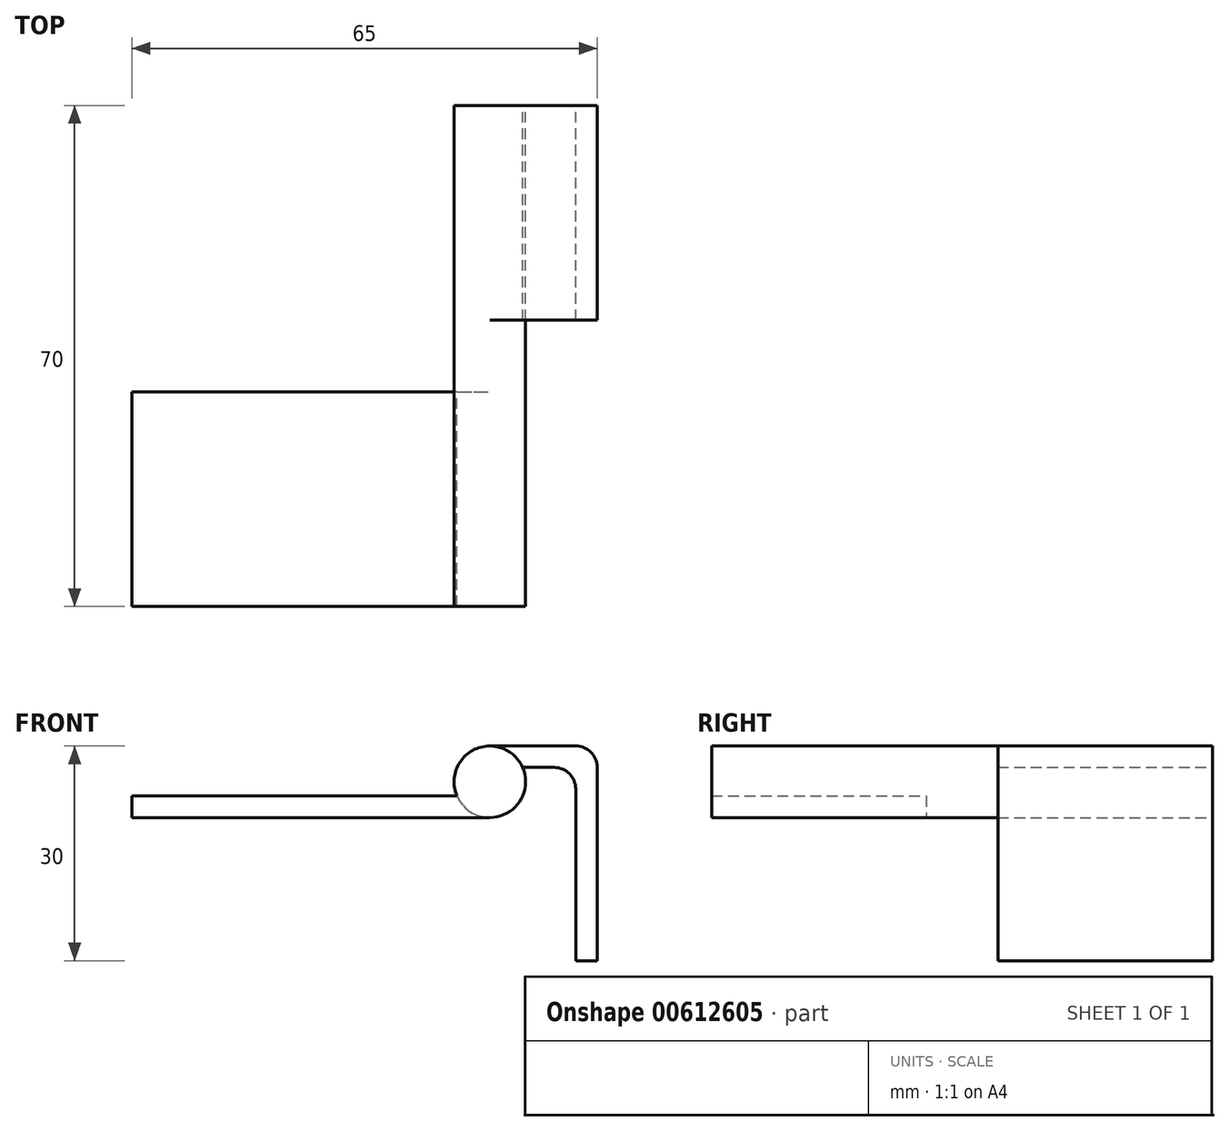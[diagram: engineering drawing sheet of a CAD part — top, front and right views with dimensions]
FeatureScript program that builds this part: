
annotation { "Feature Type Name" : "Feature", "Feature Type Description" : "" }
export const myFeature = defineFeature(function(context is Context, id is Id, definition is map)
    precondition{}
    {
        {
            var Q0;
            Q0=qCreatedBy(makeId("Front.planeOp"),FACE);
            var sketch = newSketch(context, id + "F0", { "sketchPlane" : qUnion([Q0])});
            skCircle(sketch, "E0", {"center": v(0, 0) * mm, "radius": 5 * mm});
            skLineSegment(sketch, "E1.0", {"start": v(0, 2) * mm, "end": v(9, 2) * mm});
            skLineSegment(sketch, "E2.0", {"start": v(0, 5) * mm, "end": v(12, 5) * mm});
            skLineSegment(sketch, "E3", {"start": v(0, 5) * mm, "end": v(0, 2) * mm});
            skLineSegment(sketch, "E4", {"start": v(15, 2) * mm, "end": v(15, 2) * mm});
            skLineSegment(sketch, "E5", {"start": v(-2, -70) * mm, "end": v(-5, -70) * mm});
            skLineSegment(sketch, "E6", {"start": v(15, -3) * mm, "end": v(15, -25) * mm});
            skLineSegment(sketch, "E7", {"start": v(15, -25) * mm, "end": v(12, -25) * mm});
            skLineSegment(sketch, "E8", {"start": v(12, -25) * mm, "end": v(12, -1) * mm});
            skPoint(sketch, "E9.newPointB", {"position": v(15, 2) * mm});
            skArc(sketch, "E9.filletArc", {"start": v(12, -1) * mm, "mid": v(11.12, 1.12) * mm, "end": v(9, 2) * mm});
            skPoint(sketch, "E10.visualSharp", {"position": v(15, 5) * mm});
            skArc(sketch, "E10.filletArc", {"start": v(15, 2) * mm, "mid": v(14.12, 4.12) * mm, "end": v(12, 5) * mm});
            skLineSegment(sketch, "E11", {"start": v(15, -3) * mm, "end": v(15, 2) * mm});
            skSolve(sketch);
        }
        {
            var Q0;
            {var subQ0=sQuery(id+"F0.wireOp",EDGE,"E3");Q0=makeQuery(id+"F0.imprint","IMPRINT",FACE,{"disambiguationData":[TD([[makeQuery(id+"F0.imprint","IMPRINT",EDGE,{"derivedFrom":subQ0}),-1.0]])]});}
            var Q1;
            {var subQ0=sQuery(id+"F0.wireOp",EDGE,"E3");Q1=makeQuery(id+"F0.imprint","IMPRINT",FACE,{"disambiguationData":[TD([[makeQuery(id+"F0.imprint","IMPRINT",EDGE,{"derivedFrom":subQ0}),1.0]])]});}
            extrude(context, id + "F1", {"entities" : qUnion([Q0, Q1]), "depth" : 70 * mm, "offsetDistance" : 25.4 * mm});
        }
        {
            var Q0;
            {var subQ0=sQuery(id+"F0.wireOp",EDGE,"E2.0");Q0=makeQuery(id+"F0.imprint","IMPRINT",FACE,{"disambiguationData":[TD([[makeQuery(id+"F0.imprint","IMPRINT",EDGE,{"derivedFrom":subQ0}),-1.0]])]});}
            extrude(context, id + "F2", {"entities" : qUnion([Q0]), "operationType" : NewBodyOperationType.ADD, "depth" : 30 * mm, "offsetDistance" : 25.4 * mm});
        }
        {
            var Q0;
            Q0=makeQuery(id+"F1.opExtrude","CAP_FACE",FACE,{"disambiguationData":[OSD([sQuery(id+"F0.wireOp",EDGE,"E0")])],"isStart":false});
            var sketch = newSketch(context, id + "F3", { "sketchPlane" : qUnion([Q0])});
            skLineSegment(sketch, "E12", {"start": v(0, -2) * mm, "end": v(-50, -2) * mm});
            skLineSegment(sketch, "E13", {"start": v(-50, -5) * mm, "end": v(0, -5) * mm});
            skLineSegment(sketch, "E14", {"start": v(-50, -2) * mm, "end": v(-50, -5) * mm});
            skLineSegment(sketch, "E15", {"start": v(0, -2) * mm, "end": v(0, -5) * mm});
            skSolve(sketch);
        }
        {
            var Q0;
            {var subQ0=sQuery(id+"F3.wireOp",EDGE,"E12");Q0=makeQuery(id+"F3.imprint","IMPRINT",FACE,{"disambiguationData":[TD([[makeQuery(id+"F3.imprint","IMPRINT",EDGE,{"derivedFrom":subQ0}),1.0]])]});}
            var Q1;
            {var subQ4=sQuery(id+"F3.wireOp",EDGE,"E13");Q1=makeQuery(id+"F3.imprint","IMPRINT",FACE,{"disambiguationData":[TD([[makeQuery(id+"F3.imprint","IMPRINT",EDGE,{"derivedFrom":subQ4}),1.0]])]});}
            extrude(context, id + "F4", {"entities" : qUnion([Q0, Q1]), "operationType" : NewBodyOperationType.ADD, "oppositeDirection" : true, "depth" : 30 * mm, "offsetDistance" : 25.4 * mm});
        }
    });
